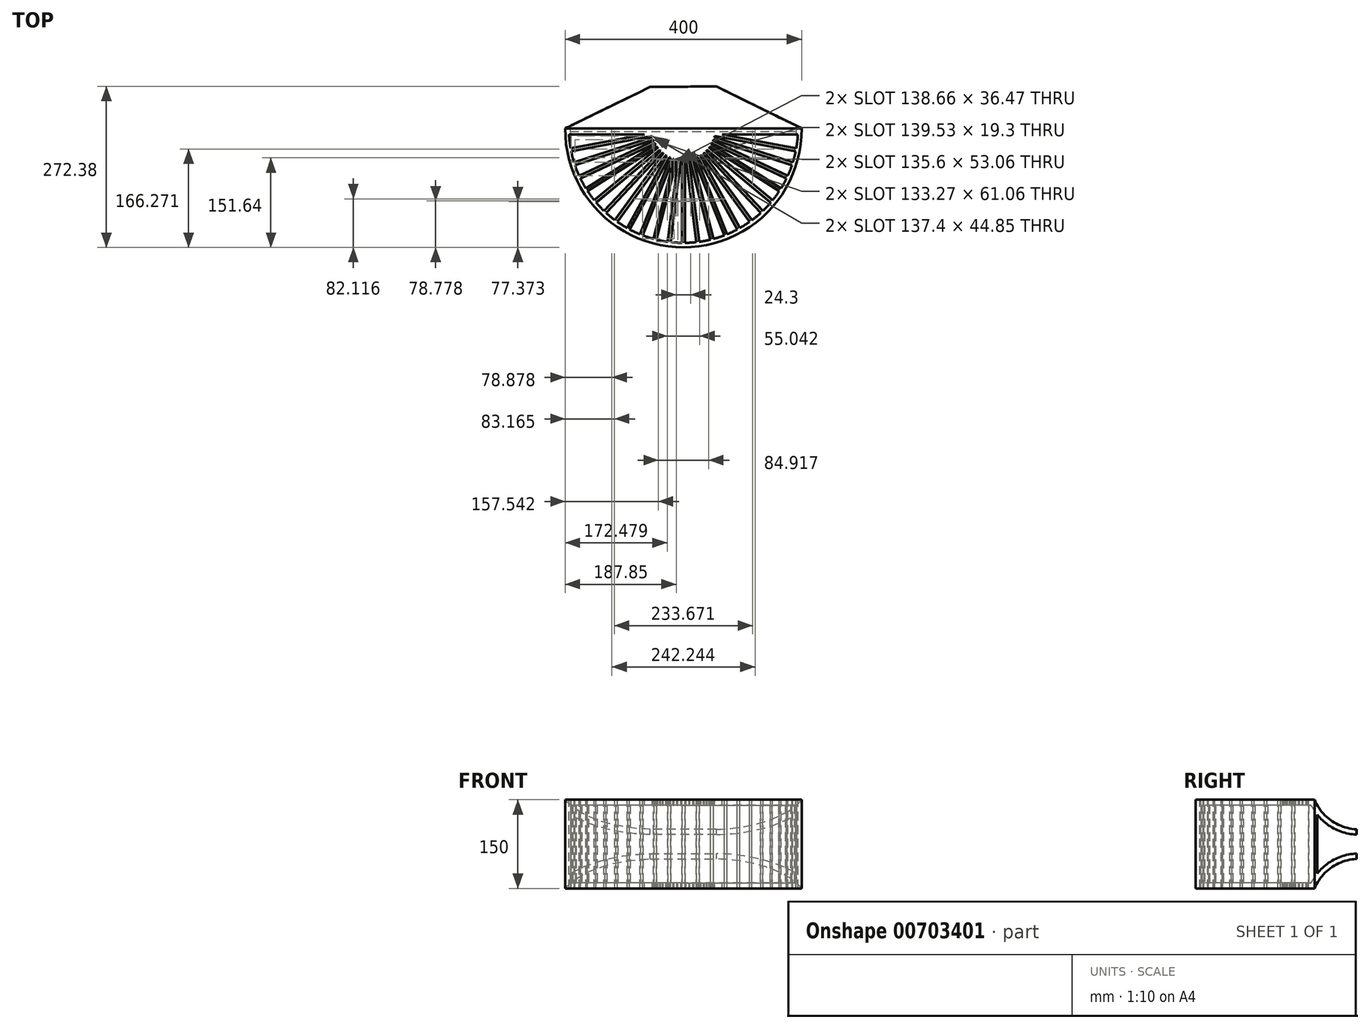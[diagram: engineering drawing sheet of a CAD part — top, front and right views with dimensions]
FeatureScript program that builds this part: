
annotation { "Feature Type Name" : "Feature", "Feature Type Description" : "" }
export const myFeature = defineFeature(function(context is Context, id is Id, definition is map)
    precondition{}
    {
        {
            var Q0;
            Q0=qCreatedBy(makeId("Top.planeOp"),FACE);
            var sketch = newSketch(context, id + "F0", { "sketchPlane" : qUnion([Q0])});
            skLineSegment(sketch, "E0", {"start": v(0, 0) * mm, "end": v(400, 0) * mm});
            skArc(sketch, "E1", {"start": v(0, 0) * mm, "mid": v(200, -201.33) * mm, "end": v(400, 0) * mm});
            skLineSegment(sketch, "E2", {"start": v(400, 0) * mm, "end": v(399.5, 75) * mm});
            skLineSegment(sketch, "E3", {"start": v(399.5, 75) * mm, "end": v(0, 72.35) * mm});
            skLineSegment(sketch, "E4", {"start": v(0, 72.35) * mm, "end": v(0, 0) * mm});
            skSolve(sketch);
        }
        {
            var Q0;
            Q0=makeQuery(id+"F0.imprint","IMPRINT",FACE,{"disambiguationData":[TD([[makeQuery(id+"F0.imprint","IMPRINT",EDGE,{"derivedFrom":sQuery(id+"F0.wireOp",EDGE,"E0")}),1.0]])]});
            var Q1;
            Q1=makeQuery(id+"F0.imprint","IMPRINT",FACE,{"disambiguationData":[TD([[makeQuery(id+"F0.imprint","IMPRINT",EDGE,{"derivedFrom":sQuery(id+"F0.wireOp",EDGE,"E0")}),-1.0]])]});
            extrude(context, id + "F1", {"entities" : qUnion([Q0, Q1]), "depth" : 150 * mm, "offsetDistance" : 25 * mm});
        }
        {
            var Q0;
            Q0=makeQuery(id+"F1.opExtrude","CAP_FACE",FACE,{"disambiguationData":[OSD([sQuery(id+"F0.wireOp",EDGE,"E1"),sQuery(id+"F0.wireOp",EDGE,"E2"),sQuery(id+"F0.wireOp",EDGE,"E3"),sQuery(id+"F0.wireOp",EDGE,"E4")])],"isStart":false});
            var sketch = newSketch(context, id + "F2", { "sketchPlane" : qUnion([Q0])});
            skLineSegment(sketch, "E5", {"start": v(249.75, 74) * mm, "end": v(400, 0) * mm});
            skLineSegment(sketch, "E6", {"start": v(400, 0) * mm, "end": v(399.5, 75) * mm});
            skLineSegment(sketch, "E7", {"start": v(399.5, 75) * mm, "end": v(249.75, 74) * mm});
            skLineSegment(sketch, "E8", {"start": v(0, 0) * mm, "end": v(0, 72.35) * mm});
            skLineSegment(sketch, "E9", {"start": v(0, 72.35) * mm, "end": v(150, 73.35) * mm});
            skLineSegment(sketch, "E10", {"start": v(150, 73.35) * mm, "end": v(0, 0) * mm});
            skSolve(sketch);
        }
        {
            var Q0;
            Q0=makeQuery(id+"F1.opExtrude","SWEPT_FACE",FACE,{"disambiguationData":[OSD([sQuery(id+"F0.wireOp",EDGE,"E4")])]});
            var sketch = newSketch(context, id + "F3", { "sketchPlane" : qUnion([Q0])});
            skLineSegment(sketch, "E11", {"start": v(-72.35, 75) * mm, "end": v(-72.35, 100) * mm});
            skLineSegment(sketch, "E12", {"start": v(-72.35, 75) * mm, "end": v(-72.35, 50) * mm});
            skArc(sketch, "E13", {"start": v(0, 0) * mm, "mid": v(-28.8, 35.66) * mm, "end": v(-72.35, 50) * mm});
            skArc(sketch, "E14", {"start": v(-72.35, 100) * mm, "mid": v(-28.8, 114.34) * mm, "end": v(0, 150) * mm});
            skLineSegment(sketch, "E15", {"start": v(-72.35, 50) * mm, "end": v(-72.35, 0) * mm});
            skLineSegment(sketch, "E16", {"start": v(-72.35, 0) * mm, "end": v(0, 0) * mm});
            skLineSegment(sketch, "E17", {"start": v(-72.35, 100) * mm, "end": v(-72.35, 150) * mm});
            skLineSegment(sketch, "E18", {"start": v(-72.35, 150) * mm, "end": v(0, 150) * mm});
            skSolve(sketch);
        }
        {
            var Q0;
            Q0 = qSketchRegion(id + "F3", true);
            extrude(context, id + "F4", {"entities" : qUnion([Q0]), "operationType" : NewBodyOperationType.REMOVE, "endBound" : BoundingType.UP_TO_NEXT, "oppositeDirection" : true, "depth" : 25 * mm, "offsetDistance" : 25 * mm});
        }
        {
            var Q0;
            Q0=makeQuery(id+"F1.opExtrude","SWEPT_FACE",FACE,{"disambiguationData":[OSD([sQuery(id+"F0.wireOp",EDGE,"E3")])]});
            var sketch = newSketch(context, id + "F5", { "sketchPlane" : qUnion([Q0])});
            skLineSegment(sketch, "E19.bottom", {"start": v(0, 0) * mm, "end": v(-400, 0) * mm});
            skLineSegment(sketch, "E19.top", {"start": v(0, 150) * mm, "end": v(-400, 150) * mm});
            skLineSegment(sketch, "E19.left", {"start": v(0, 0) * mm, "end": v(0, 150) * mm});
            skLineSegment(sketch, "E19.right", {"start": v(-400, 0) * mm, "end": v(-400, 150) * mm});
            skSolve(sketch);
        }
        {
            var Q0;
            Q0 = qSketchRegion(id + "F5", true);
            extrude(context, id + "F6", {"entities" : qUnion([Q0]), "operationType" : NewBodyOperationType.REMOVE, "oppositeDirection" : true, "depth" : 3 * mm, "offsetDistance" : 25 * mm});
        }
        {
            var Q0;
            Q0 = qSketchRegion(id + "F2", true);
            var Q1;
            {var subQ0=sQuery(id+"F0.wireOp",EDGE,"E1");var subQ1=sQuery(id+"F0.wireOp",EDGE,"E4");var subQ2=sQuery(id+"F0.wireOp",EDGE,"E2");Q1=makeQuery(id+"F4.boolean.opBoolean","SPLIT",FACE,{"disambiguationData":[TD([makeQuery(id+"F1.opExtrude","SWEPT_FACE",FACE,{"disambiguationData":[OSD([subQ0])]})])],"derivedFrom":makeQuery(id+"F1.opExtrude","CAP_FACE",FACE,{"disambiguationData":[OSD([subQ0,subQ2,sQuery(id+"F0.wireOp",EDGE,"E3"),subQ1])],"isStart":true})});}
            extrude(context, id + "F7", {"entities" : qUnion([Q0]), "operationType" : NewBodyOperationType.REMOVE, "endBound" : BoundingType.UP_TO_SURFACE, "oppositeDirection" : true, "depth" : 25 * mm, "endBoundEntityFace" : qUnion([Q1]), "offsetDistance" : 25 * mm});
        }
        {
            var Q0;
            Q0=makeQuery(id+"F6.boolean.opBoolean","COPY",FACE,{"derivedFrom":makeQuery(id+"F6.opExtrude","CAP_FACE",FACE,{"disambiguationData":[OSD([sQuery(id+"F5.wireOp",EDGE,"E19.bottom"),sQuery(id+"F5.wireOp",EDGE,"E19.top"),sQuery(id+"F5.wireOp",EDGE,"E19.left"),sQuery(id+"F5.wireOp",EDGE,"E19.right")])],"isStart":false})});
            var Q1;
            Q1=makeQuery(id+"F7.boolean.opBoolean","COPY",FACE,{"derivedFrom":makeQuery(id+"F7.opExtrude","SWEPT_FACE",FACE,{"disambiguationData":[OSD([sQuery(id+"F2.wireOp",EDGE,"E10")])]})});
            var Q2;
            Q2=makeQuery(id+"F7.boolean.opBoolean","COPY",FACE,{"derivedFrom":makeQuery(id+"F7.opExtrude","SWEPT_FACE",FACE,{"disambiguationData":[OSD([sQuery(id+"F2.wireOp",EDGE,"E5")])]})});
            shell(context, id + "F8", {"entities" : qUnion([Q0, Q1, Q2]), "thickness" : 9 * mm});
        }
        {
            var Q0;
            {var subQ0=sQuery(id+"F0.wireOp",EDGE,"E1");var subQ1=sQuery(id+"F0.wireOp",EDGE,"E4");var subQ2=sQuery(id+"F0.wireOp",EDGE,"E2");Q0=makeQuery(id+"F4.boolean.opBoolean","SPLIT",FACE,{"disambiguationData":[TD([makeQuery(id+"F1.opExtrude","SWEPT_FACE",FACE,{"disambiguationData":[OSD([subQ0])]})])],"derivedFrom":makeQuery(id+"F1.opExtrude","CAP_FACE",FACE,{"disambiguationData":[OSD([subQ0,subQ2,sQuery(id+"F0.wireOp",EDGE,"E3"),subQ1])],"isStart":false})});}
            var sketch = newSketch(context, id + "F9", { "sketchPlane" : qUnion([Q0])});
            skCircle(sketch, "E20.cCircle", {"center": v(200, 0) * mm, "radius": 201.33 * mm, "construction": true});
            skLineSegment(sketch, "E20.0", {"start": v(200, -201.33) * mm, "end": v(174.77, -199.74) * mm});
            skLineSegment(sketch, "E20.1", {"start": v(174.77, -199.74) * mm, "end": v(149.93, -195) * mm});
            skLineSegment(sketch, "E20.2", {"start": v(149.93, -195) * mm, "end": v(125.89, -187.2) * mm});
            skLineSegment(sketch, "E20.3", {"start": v(125.89, -187.2) * mm, "end": v(103, -176.43) * mm});
            skLineSegment(sketch, "E20.4", {"start": v(103, -176.43) * mm, "end": v(81.66, -162.88) * mm});
            skLineSegment(sketch, "E20.5", {"start": v(81.66, -162.88) * mm, "end": v(62.18, -146.76) * mm});
            skLineSegment(sketch, "E20.6", {"start": v(62.18, -146.76) * mm, "end": v(44.87, -128.33) * mm});
            skLineSegment(sketch, "E20.7", {"start": v(44.87, -128.33) * mm, "end": v(30.01, -107.88) * mm});
            skLineSegment(sketch, "E20.8", {"start": v(30.01, -107.88) * mm, "end": v(17.83, -85.72) * mm});
            skLineSegment(sketch, "E20.9", {"start": v(17.83, -85.72) * mm, "end": v(8.53, -62.21) * mm});
            skLineSegment(sketch, "E20.10", {"start": v(8.53, -62.21) * mm, "end": v(2.24, -37.73) * mm});
            skLineSegment(sketch, "E20.11", {"start": v(2.24, -37.73) * mm, "end": v(-0.93, -12.64) * mm});
            skLineSegment(sketch, "E20.12", {"start": v(-0.93, -12.64) * mm, "end": v(-0.93, 12.64) * mm});
            skLineSegment(sketch, "E20.13", {"start": v(-0.93, 12.64) * mm, "end": v(2.24, 37.73) * mm});
            skLineSegment(sketch, "E20.14", {"start": v(2.24, 37.73) * mm, "end": v(8.53, 62.21) * mm});
            skLineSegment(sketch, "E20.15", {"start": v(8.53, 62.21) * mm, "end": v(17.83, 85.72) * mm});
            skLineSegment(sketch, "E20.16", {"start": v(17.83, 85.72) * mm, "end": v(30.01, 107.88) * mm});
            skLineSegment(sketch, "E20.17", {"start": v(30.01, 107.88) * mm, "end": v(44.87, 128.33) * mm});
            skLineSegment(sketch, "E20.18", {"start": v(44.87, 128.33) * mm, "end": v(62.18, 146.76) * mm});
            skLineSegment(sketch, "E20.19", {"start": v(62.18, 146.76) * mm, "end": v(81.66, 162.88) * mm});
            skLineSegment(sketch, "E20.20", {"start": v(81.66, 162.88) * mm, "end": v(103, 176.43) * mm});
            skLineSegment(sketch, "E20.21", {"start": v(103, 176.43) * mm, "end": v(125.89, 187.2) * mm});
            skLineSegment(sketch, "E20.22", {"start": v(125.89, 187.2) * mm, "end": v(149.93, 195) * mm});
            skLineSegment(sketch, "E20.23", {"start": v(149.93, 195) * mm, "end": v(174.77, 199.74) * mm});
            skLineSegment(sketch, "E20.24", {"start": v(174.77, 199.74) * mm, "end": v(200, 201.33) * mm});
            skLineSegment(sketch, "E20.25", {"start": v(200, 201.33) * mm, "end": v(225.23, 199.74) * mm});
            skLineSegment(sketch, "E20.26", {"start": v(225.23, 199.74) * mm, "end": v(250.07, 195) * mm});
            skLineSegment(sketch, "E20.27", {"start": v(250.07, 195) * mm, "end": v(274.11, 187.2) * mm});
            skLineSegment(sketch, "E20.28", {"start": v(274.11, 187.2) * mm, "end": v(297, 176.43) * mm});
            skLineSegment(sketch, "E20.29", {"start": v(297, 176.43) * mm, "end": v(318.34, 162.88) * mm});
            skLineSegment(sketch, "E20.30", {"start": v(318.34, 162.88) * mm, "end": v(337.82, 146.76) * mm});
            skLineSegment(sketch, "E20.31", {"start": v(337.82, 146.76) * mm, "end": v(355.13, 128.33) * mm});
            skLineSegment(sketch, "E20.32", {"start": v(355.13, 128.33) * mm, "end": v(369.99, 107.88) * mm});
            skLineSegment(sketch, "E20.33", {"start": v(369.99, 107.88) * mm, "end": v(382.17, 85.72) * mm});
            skLineSegment(sketch, "E20.34", {"start": v(382.17, 85.72) * mm, "end": v(391.47, 62.21) * mm});
            skLineSegment(sketch, "E20.35", {"start": v(391.47, 62.21) * mm, "end": v(397.76, 37.73) * mm});
            skLineSegment(sketch, "E20.36", {"start": v(397.76, 37.73) * mm, "end": v(400.93, 12.64) * mm});
            skLineSegment(sketch, "E20.37", {"start": v(400.93, 12.64) * mm, "end": v(400.93, -12.64) * mm});
            skLineSegment(sketch, "E20.38", {"start": v(400.93, -12.64) * mm, "end": v(397.76, -37.73) * mm});
            skLineSegment(sketch, "E20.39", {"start": v(397.76, -37.73) * mm, "end": v(391.47, -62.21) * mm});
            skLineSegment(sketch, "E20.40", {"start": v(391.47, -62.21) * mm, "end": v(382.17, -85.72) * mm});
            skLineSegment(sketch, "E20.41", {"start": v(382.17, -85.72) * mm, "end": v(369.99, -107.88) * mm});
            skLineSegment(sketch, "E20.42", {"start": v(369.99, -107.88) * mm, "end": v(355.13, -128.33) * mm});
            skLineSegment(sketch, "E20.43", {"start": v(355.13, -128.33) * mm, "end": v(337.82, -146.76) * mm});
            skLineSegment(sketch, "E20.44", {"start": v(337.82, -146.76) * mm, "end": v(318.34, -162.88) * mm});
            skLineSegment(sketch, "E20.45", {"start": v(318.34, -162.88) * mm, "end": v(297, -176.43) * mm});
            skLineSegment(sketch, "E20.46", {"start": v(297, -176.43) * mm, "end": v(274.11, -187.2) * mm});
            skLineSegment(sketch, "E20.47", {"start": v(274.11, -187.2) * mm, "end": v(250.07, -195) * mm});
            skLineSegment(sketch, "E20.48", {"start": v(250.07, -195) * mm, "end": v(225.23, -199.74) * mm});
            skLineSegment(sketch, "E20.49", {"start": v(225.23, -199.74) * mm, "end": v(200, -201.33) * mm});
            skArc(sketch, "E21", {"start": v(254.36, 0) * mm, "mid": v(200, -54.36) * mm, "end": v(145.64, 0) * mm});
            skLineSegment(sketch, "E22", {"start": v(292.96, -5.85) * mm, "end": v(293.27, -0.86) * mm});
            skLineSegment(sketch, "E23", {"start": v(185.9, 0) * mm, "end": v(185.9, -10) * mm});
            skLineSegment(sketch, "E24", {"start": v(185.9, -10) * mm, "end": v(0.19, -10.05) * mm});
            skLineSegment(sketch, "E25", {"start": v(185.9, -10) * mm, "end": v(279.98, -10) * mm});
            skLineSegment(sketch, "E26", {"start": v(279.98, -10) * mm, "end": v(400, -10) * mm});
            skArc(sketch, "E27", {"start": v(393.74, 0) * mm, "mid": v(200, -193.74) * mm, "end": v(6.26, 0) * mm});
            skLineSegment(sketch, "E28", {"start": v(253.81, -7.72) * mm, "end": v(390.76, -33.84) * mm});
            skLineSegment(sketch, "E29", {"start": v(252.88, -12.63) * mm, "end": v(389.82, -38.76) * mm});
            skLineSegment(sketch, "E30", {"start": v(252.42, -14.4) * mm, "end": v(385.01, -57.49) * mm});
            skLineSegment(sketch, "E31", {"start": v(250.88, -19.16) * mm, "end": v(383.47, -62.24) * mm});
            skLineSegment(sketch, "E32", {"start": v(250.2, -20.86) * mm, "end": v(376.35, -80.22) * mm});
            skLineSegment(sketch, "E33", {"start": v(248.07, -25.38) * mm, "end": v(374.22, -84.75) * mm});
            skLineSegment(sketch, "E34", {"start": v(247.2, -26.99) * mm, "end": v(364.9, -101.7) * mm});
            skLineSegment(sketch, "E35", {"start": v(244.51, -31.2) * mm, "end": v(362.23, -105.91) * mm});
            skLineSegment(sketch, "E36", {"start": v(243.44, -32.69) * mm, "end": v(350.86, -121.56) * mm});
            skLineSegment(sketch, "E37", {"start": v(240.25, -36.54) * mm, "end": v(347.67, -125.4) * mm});
            skLineSegment(sketch, "E38", {"start": v(235.35, -41.3) * mm, "end": v(330.8, -142.93) * mm});
            skLineSegment(sketch, "E39", {"start": v(239, -37.88) * mm, "end": v(334.43, -139.5) * mm});
            skLineSegment(sketch, "E40", {"start": v(233.94, -42.46) * mm, "end": v(315.9, -155.26) * mm});
            skLineSegment(sketch, "E41", {"start": v(229.9, -45.4) * mm, "end": v(311.84, -158.2) * mm});
            skLineSegment(sketch, "E42", {"start": v(223.97, -48.8) * mm, "end": v(291.14, -170.97) * mm});
            skLineSegment(sketch, "E43", {"start": v(228.35, -46.38) * mm, "end": v(295.52, -168.56) * mm});
            skLineSegment(sketch, "E44", {"start": v(217.67, -51.41) * mm, "end": v(268.99, -181.04) * mm});
            skLineSegment(sketch, "E45", {"start": v(222.32, -49.57) * mm, "end": v(273.64, -179.2) * mm});
            skLineSegment(sketch, "E46", {"start": v(211.08, -53.22) * mm, "end": v(245.76, -188.26) * mm});
            skLineSegment(sketch, "E47", {"start": v(215.93, -51.98) * mm, "end": v(250.6, -187.02) * mm});
            skLineSegment(sketch, "E48", {"start": v(204.33, -54.2) * mm, "end": v(221.8, -192.5) * mm});
            skLineSegment(sketch, "E49", {"start": v(209.29, -53.56) * mm, "end": v(226.76, -191.88) * mm});
            skLineSegment(sketch, "E50.MirrorCS", {"start": v(195.67, -54.2) * mm, "end": v(178.2, -192.5) * mm});
            skLineSegment(sketch, "E51.MirrorCS", {"start": v(190.71, -53.56) * mm, "end": v(173.24, -191.88) * mm});
            skLineSegment(sketch, "E52.MirrorCS", {"start": v(188.92, -53.22) * mm, "end": v(154.24, -188.26) * mm});
            skLineSegment(sketch, "E53.MirrorCS", {"start": v(184.07, -51.98) * mm, "end": v(149.4, -187.02) * mm});
            skLineSegment(sketch, "E54.MirrorCS", {"start": v(182.33, -51.41) * mm, "end": v(131.01, -181.04) * mm});
            skLineSegment(sketch, "E55.MirrorCS", {"start": v(177.68, -49.57) * mm, "end": v(126.36, -179.2) * mm});
            skLineSegment(sketch, "E56.MirrorCS", {"start": v(152.8, -26.99) * mm, "end": v(35.1, -101.7) * mm});
            skLineSegment(sketch, "E57.MirrorCS", {"start": v(164.65, -41.3) * mm, "end": v(69.2, -142.93) * mm});
            skLineSegment(sketch, "E58.MirrorCS", {"start": v(159.75, -36.54) * mm, "end": v(52.33, -125.4) * mm});
            skLineSegment(sketch, "E59.MirrorCS", {"start": v(151.93, -25.38) * mm, "end": v(25.78, -84.75) * mm});
            skLineSegment(sketch, "E60.MirrorCS", {"start": v(156.56, -32.69) * mm, "end": v(49.14, -121.56) * mm});
            skLineSegment(sketch, "E61.MirrorCS", {"start": v(166.06, -42.46) * mm, "end": v(84.1, -155.26) * mm});
            skLineSegment(sketch, "E62.MirrorCS", {"start": v(149.12, -19.16) * mm, "end": v(16.53, -62.24) * mm});
            skLineSegment(sketch, "E63.MirrorCS", {"start": v(147.12, -12.63) * mm, "end": v(10.18, -38.76) * mm});
            skLineSegment(sketch, "E64.MirrorCS", {"start": v(170.1, -45.4) * mm, "end": v(88.16, -158.2) * mm});
            skLineSegment(sketch, "E65.MirrorCS", {"start": v(176.03, -48.8) * mm, "end": v(108.86, -170.97) * mm});
            skLineSegment(sketch, "E66.MirrorCS", {"start": v(146.19, -7.72) * mm, "end": v(9.24, -33.84) * mm});
            skLineSegment(sketch, "E67.MirrorCS", {"start": v(155.49, -31.2) * mm, "end": v(37.77, -105.91) * mm});
            skLineSegment(sketch, "E68.MirrorCS", {"start": v(171.65, -46.38) * mm, "end": v(104.48, -168.56) * mm});
            skLineSegment(sketch, "E69.MirrorCS", {"start": v(149.8, -20.86) * mm, "end": v(23.65, -80.22) * mm});
            skLineSegment(sketch, "E70.MirrorCS", {"start": v(161, -37.88) * mm, "end": v(65.57, -139.5) * mm});
            skLineSegment(sketch, "E71.MirrorCS", {"start": v(147.58, -14.4) * mm, "end": v(14.99, -57.49) * mm});
            skLineSegment(sketch, "E72", {"start": v(202.5, -54.3) * mm, "end": v(202.5, -193.72) * mm});
            skLineSegment(sketch, "E73", {"start": v(197.5, -54.3) * mm, "end": v(197.5, -193.72) * mm});
            skSolve(sketch);
        }
        {
            var Q0;
            {var subQ0=sQuery(id+"F9.wireOp",EDGE,"E26");var subQ1=sQuery(id+"F9.wireOp",EDGE,"E25");var subQ2=makeQuery(id+"F9.imprint","INTERSECT",VERTEX,{"derivedFrom":[subQ1,subQ0]});Q0=makeQuery(id+"F9.imprint","IMPRINT",FACE,{"disambiguationData":[TD([[makeQuery(id+"F9.imprint","IMPRINT",EDGE,{"disambiguationData":[TD([[subQ2,1.0]])],"derivedFrom":subQ1}),-1.0]])]});}
            var Q1;
            {var subQ0=sQuery(id+"F9.wireOp",EDGE,"E66.MirrorCS");var subQ1=sQuery(id+"F9.wireOp",EDGE,"E24");var subQ2=makeQuery(id+"F9.imprint","INTERSECT",VERTEX,{"derivedFrom":[subQ1,subQ0]});Q1=makeQuery(id+"F9.imprint","IMPRINT",FACE,{"disambiguationData":[TD([[makeQuery(id+"F9.imprint","IMPRINT",EDGE,{"disambiguationData":[TD([[subQ2,-1.0]])],"derivedFrom":subQ1}),1.0]])]});}
            var Q2;
            {var subQ0=sQuery(id+"F9.wireOp",EDGE,"E63.MirrorCS");Q2=makeQuery(id+"F9.imprint","IMPRINT",FACE,{"disambiguationData":[TD([[makeQuery(id+"F9.imprint","IMPRINT",EDGE,{"derivedFrom":subQ0}),1.0]])]});}
            var Q3;
            {var subQ0=sQuery(id+"F9.wireOp",EDGE,"E62.MirrorCS");Q3=makeQuery(id+"F9.imprint","IMPRINT",FACE,{"disambiguationData":[TD([[makeQuery(id+"F9.imprint","IMPRINT",EDGE,{"derivedFrom":subQ0}),1.0]])]});}
            var Q4;
            {var subQ0=sQuery(id+"F9.wireOp",EDGE,"E56.MirrorCS");Q4=makeQuery(id+"F9.imprint","IMPRINT",FACE,{"disambiguationData":[TD([[makeQuery(id+"F9.imprint","IMPRINT",EDGE,{"derivedFrom":subQ0}),-1.0]])]});}
            var Q5;
            {var subQ0=sQuery(id+"F9.wireOp",EDGE,"E60.MirrorCS");Q5=makeQuery(id+"F9.imprint","IMPRINT",FACE,{"disambiguationData":[TD([[makeQuery(id+"F9.imprint","IMPRINT",EDGE,{"derivedFrom":subQ0}),-1.0]])]});}
            var Q6;
            {var subQ0=sQuery(id+"F9.wireOp",EDGE,"E58.MirrorCS");Q6=makeQuery(id+"F9.imprint","IMPRINT",FACE,{"disambiguationData":[TD([[makeQuery(id+"F9.imprint","IMPRINT",EDGE,{"derivedFrom":subQ0}),1.0]])]});}
            var Q7;
            {var subQ0=sQuery(id+"F9.wireOp",EDGE,"E57.MirrorCS");Q7=makeQuery(id+"F9.imprint","IMPRINT",FACE,{"disambiguationData":[TD([[makeQuery(id+"F9.imprint","IMPRINT",EDGE,{"derivedFrom":subQ0}),1.0]])]});}
            var Q8;
            {var subQ0=sQuery(id+"F9.wireOp",EDGE,"E64.MirrorCS");Q8=makeQuery(id+"F9.imprint","IMPRINT",FACE,{"disambiguationData":[TD([[makeQuery(id+"F9.imprint","IMPRINT",EDGE,{"derivedFrom":subQ0}),1.0]])]});}
            var Q9;
            {var subQ0=sQuery(id+"F9.wireOp",EDGE,"E55.MirrorCS");Q9=makeQuery(id+"F9.imprint","IMPRINT",FACE,{"disambiguationData":[TD([[makeQuery(id+"F9.imprint","IMPRINT",EDGE,{"derivedFrom":subQ0}),-1.0]])]});}
            var Q10;
            {var subQ0=sQuery(id+"F9.wireOp",EDGE,"E53.MirrorCS");Q10=makeQuery(id+"F9.imprint","IMPRINT",FACE,{"disambiguationData":[TD([[makeQuery(id+"F9.imprint","IMPRINT",EDGE,{"derivedFrom":subQ0}),-1.0]])]});}
            var Q11;
            {var subQ0=sQuery(id+"F9.wireOp",EDGE,"E51.MirrorCS");Q11=makeQuery(id+"F9.imprint","IMPRINT",FACE,{"disambiguationData":[TD([[makeQuery(id+"F9.imprint","IMPRINT",EDGE,{"derivedFrom":subQ0}),-1.0]])]});}
            var Q12;
            {var subQ0=sQuery(id+"F9.wireOp",EDGE,"E50.MirrorCS");Q12=makeQuery(id+"F9.imprint","IMPRINT",FACE,{"disambiguationData":[TD([[makeQuery(id+"F9.imprint","IMPRINT",EDGE,{"derivedFrom":subQ0}),1.0]])]});}
            var Q13;
            {var subQ0=sQuery(id+"F9.wireOp",EDGE,"E48");Q13=makeQuery(id+"F9.imprint","IMPRINT",FACE,{"disambiguationData":[TD([[makeQuery(id+"F9.imprint","IMPRINT",EDGE,{"derivedFrom":subQ0}),-1.0]])]});}
            var Q14;
            {var subQ0=sQuery(id+"F9.wireOp",EDGE,"E46");Q14=makeQuery(id+"F9.imprint","IMPRINT",FACE,{"disambiguationData":[TD([[makeQuery(id+"F9.imprint","IMPRINT",EDGE,{"derivedFrom":subQ0}),-1.0]])]});}
            var Q15;
            {var subQ0=sQuery(id+"F9.wireOp",EDGE,"E44");Q15=makeQuery(id+"F9.imprint","IMPRINT",FACE,{"disambiguationData":[TD([[makeQuery(id+"F9.imprint","IMPRINT",EDGE,{"derivedFrom":subQ0}),-1.0]])]});}
            var Q16;
            {var subQ0=sQuery(id+"F9.wireOp",EDGE,"E42");Q16=makeQuery(id+"F9.imprint","IMPRINT",FACE,{"disambiguationData":[TD([[makeQuery(id+"F9.imprint","IMPRINT",EDGE,{"derivedFrom":subQ0}),-1.0]])]});}
            var Q17;
            {var subQ0=sQuery(id+"F9.wireOp",EDGE,"E41");Q17=makeQuery(id+"F9.imprint","IMPRINT",FACE,{"disambiguationData":[TD([[makeQuery(id+"F9.imprint","IMPRINT",EDGE,{"derivedFrom":subQ0}),-1.0]])]});}
            var Q18;
            {var subQ0=sQuery(id+"F9.wireOp",EDGE,"E38");Q18=makeQuery(id+"F9.imprint","IMPRINT",FACE,{"disambiguationData":[TD([[makeQuery(id+"F9.imprint","IMPRINT",EDGE,{"derivedFrom":subQ0}),-1.0]])]});}
            var Q19;
            {var subQ0=sQuery(id+"F9.wireOp",EDGE,"E37");Q19=makeQuery(id+"F9.imprint","IMPRINT",FACE,{"disambiguationData":[TD([[makeQuery(id+"F9.imprint","IMPRINT",EDGE,{"derivedFrom":subQ0}),-1.0]])]});}
            var Q20;
            {var subQ0=sQuery(id+"F9.wireOp",EDGE,"E35");Q20=makeQuery(id+"F9.imprint","IMPRINT",FACE,{"disambiguationData":[TD([[makeQuery(id+"F9.imprint","IMPRINT",EDGE,{"derivedFrom":subQ0}),-1.0]])]});}
            var Q21;
            {var subQ0=sQuery(id+"F9.wireOp",EDGE,"E33");Q21=makeQuery(id+"F9.imprint","IMPRINT",FACE,{"disambiguationData":[TD([[makeQuery(id+"F9.imprint","IMPRINT",EDGE,{"derivedFrom":subQ0}),-1.0]])]});}
            var Q22;
            {var subQ0=sQuery(id+"F9.wireOp",EDGE,"E31");Q22=makeQuery(id+"F9.imprint","IMPRINT",FACE,{"disambiguationData":[TD([[makeQuery(id+"F9.imprint","IMPRINT",EDGE,{"derivedFrom":subQ0}),-1.0]])]});}
            var Q23;
            {var subQ0=sQuery(id+"F9.wireOp",EDGE,"E29");Q23=makeQuery(id+"F9.imprint","IMPRINT",FACE,{"disambiguationData":[TD([[makeQuery(id+"F9.imprint","IMPRINT",EDGE,{"derivedFrom":subQ0}),-1.0]])]});}
            var Q24;
            {var subQ0=sQuery(id+"F0.wireOp",EDGE,"E1");var subQ1=sQuery(id+"F0.wireOp",EDGE,"E4");var subQ2=sQuery(id+"F0.wireOp",EDGE,"E2");Q24=makeQuery(id+"F4.boolean.opBoolean","SPLIT",FACE,{"disambiguationData":[TD([makeQuery(id+"F1.opExtrude","SWEPT_FACE",FACE,{"disambiguationData":[OSD([subQ0])]})])],"derivedFrom":makeQuery(id+"F1.opExtrude","CAP_FACE",FACE,{"disambiguationData":[OSD([subQ0,subQ2,sQuery(id+"F0.wireOp",EDGE,"E3"),subQ1])],"isStart":true})});}
            extrude(context, id + "F10", {"entities" : qUnion([Q0, Q1, Q2, Q3, Q4, Q5, Q6, Q7, Q8, Q9, Q10, Q11, Q12, Q13, Q14, Q15, Q16, Q17, Q18, Q19, Q20, Q21, Q22, Q23]), "operationType" : NewBodyOperationType.REMOVE, "endBound" : BoundingType.UP_TO_SURFACE, "oppositeDirection" : true, "depth" : 25 * mm, "endBoundEntityFace" : qUnion([Q24]), "offsetDistance" : 25 * mm});
        }
    });
